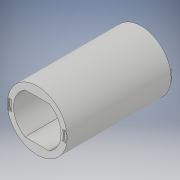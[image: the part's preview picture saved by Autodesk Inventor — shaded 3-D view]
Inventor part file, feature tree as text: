
AUTODESK INVENTOR PART (.ipt)
format: ipt  version: 2017 (Build 210142000, 142)  size: 145,408 bytes
history: native  units: in
note: dims shown in document units (in); Inventor stores cm internally (conversion verified against a paired STEP export)
features: sketch x3, extrude x2, other x1
ambient origin geometry x8: Origin, YZ Plane, XZ Plane, XY Plane, X Axis, Y Axis, Z Axis, Center Point
bodies: Solid1 (feature_tree)
feature tree (6):
  other  "corridor"
  extrude  "connection"  Depth=6.6667in
  extrude  "receive"  Depth=17.0in
  sketch  "Sketch1"  dims[d0=6.6667in d1=4.0in]
  sketch  "Sketch3"  dims[d2=1.0in d3=17.0in d4=0.0in d7=1.0in]
  sketch  "Sketch4"  dims[d12=0.25in d13=0.0in d14=0.076in d15=0.076in d16=0.076in d17=0.076in d18=0.25in d19=0.0in]
